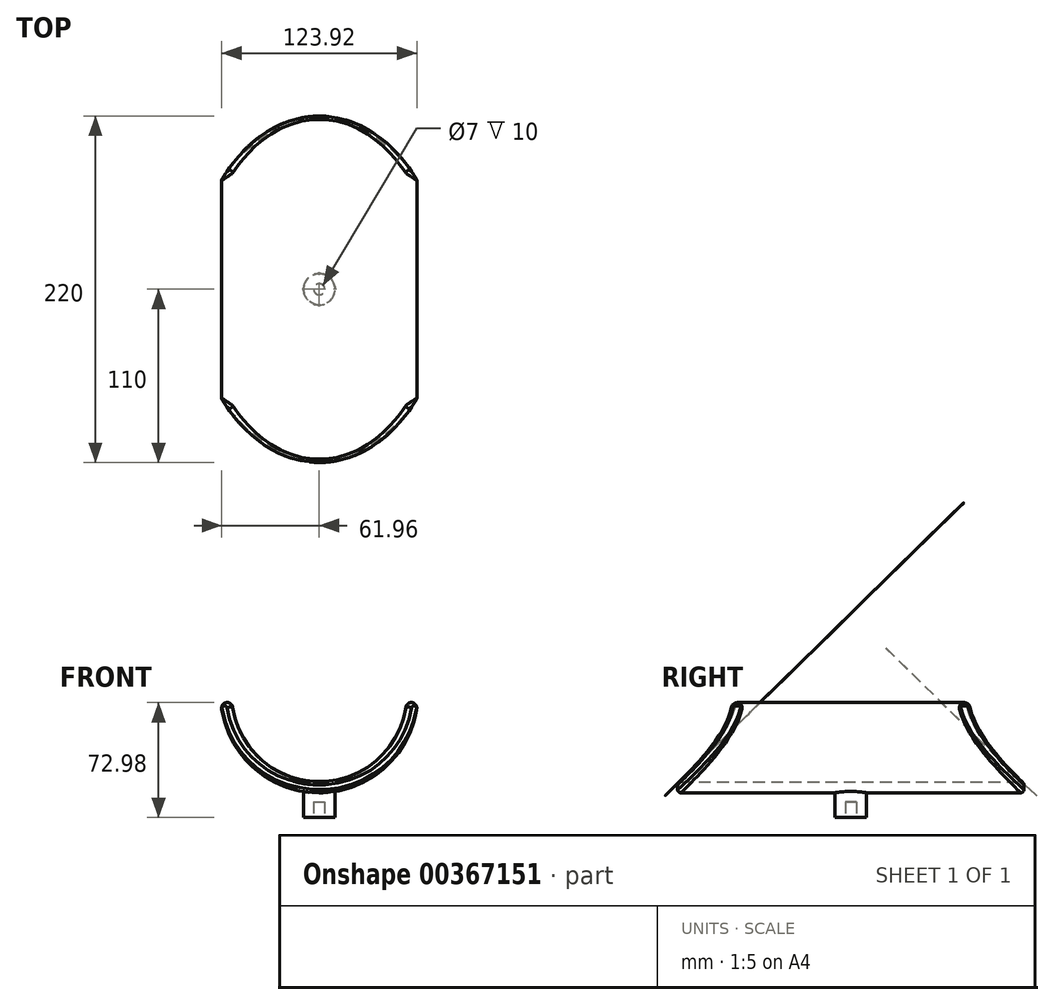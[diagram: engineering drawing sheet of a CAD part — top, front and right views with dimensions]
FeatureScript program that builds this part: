
annotation { "Feature Type Name" : "Feature", "Feature Type Description" : "" }
export const myFeature = defineFeature(function(context is Context, id is Id, definition is map)
    precondition{}
    {
        {
            var Q0;
            Q0=qCreatedBy(makeId("Top.planeOp"),FACE);
            var sketch = newSketch(context, id + "F0", { "sketchPlane" : qUnion([Q0])});
            skEllipse(sketch, "E0", {"center": v(0, 0) * mm, "majorRadius": 110 * mm, "minorRadius": 80 * mm, "majorAxis": v(0, 1)});
            skLineSegment(sketch, "E1", {"start": v(0, 0) * mm, "end": v(0, 110) * mm, "construction": true});
            skLineSegment(sketch, "E2", {"start": v(0, 0) * mm, "end": v(80, 0) * mm, "construction": true});
            skSolve(sketch);
        }
        {
            var Q0;
            Q0 = qSketchRegion(id + "F0", true);
            extrude(context, id + "F1", {"entities" : qUnion([Q0]), "endBound" : BoundingType.SYMMETRIC, "depth" : 150 * mm});
        }
        {
            var Q0;
            Q0=qCreatedBy(makeId("Front.planeOp"),FACE);
            var sketch = newSketch(context, id + "F2", { "sketchPlane" : qUnion([Q0])});
            skLineSegment(sketch, "E3", {"start": v(-80, -75) * mm, "end": v(-80, 75) * mm});
            skLineSegment(sketch, "E4", {"start": v(80, 75) * mm, "end": v(80, -75) * mm});
            skLineSegment(sketch, "E5", {"start": v(-55, 0) * mm, "end": v(55, 0) * mm, "construction": true});
            skArc(sketch, "E6", {"start": v(-55, 0) * mm, "mid": v(0, -47.31) * mm, "end": v(55, 0) * mm});
            skArc(sketch, "E7.0", {"start": v(-61.92, -1.05) * mm, "mid": v(0, -54.31) * mm, "end": v(61.92, -1.05) * mm});
            skArc(sketch, "E8", {"start": v(-61.92, -1.05) * mm, "mid": v(-58.98, 2.94) * mm, "end": v(-55, 0) * mm});
            skArc(sketch, "E9", {"start": v(61.92, -1.05) * mm, "mid": v(58.98, 2.94) * mm, "end": v(55, 0) * mm});
            skSolve(sketch);
        }
        {
            var Q0;
            Q0 = qSketchRegion(id + "F2", true);
            extrude(context, id + "F3", {"entities" : qUnion([Q0]), "operationType" : NewBodyOperationType.INTERSECT, "endBound" : BoundingType.SYMMETRIC, "depth" : 400 * mm});
        }
        {
            var Q0;
            Q0=qCreatedBy(makeId("Top.planeOp"),FACE);
            cPlane(context, id + "F4", {"entities" : qUnion([Q0]), "cplaneType" : CPlaneType.OFFSET, "offset" : 70 * mm, "oppositeDirection" : true, "width" : 150 * mm, "height" : 150 * mm});
        }
        {
            var Q0;
            Q0=qCreatedBy(id+"F4.planeOp",FACE);
            var sketch = newSketch(context, id + "F5", { "sketchPlane" : qUnion([Q0])});
            skCircle(sketch, "E10", {"center": v(0, 0) * mm, "radius": 10 * mm});
            skSolve(sketch);
        }
        {
            var Q0;
            Q0 = qSketchRegion(id + "F5", true);
            var Q1;
            Q1=makeQuery(id+"F1.opExtrude","SWEPT_BODY",BODY,{"disambiguationData":[OSD([sQuery(id+"F0.wireOp",EDGE,"E0")])]});
            extrude(context, id + "F6", {"entities" : qUnion([Q0]), "operationType" : NewBodyOperationType.ADD, "endBound" : BoundingType.UP_TO_BODY, "endBoundEntityBody" : qUnion([Q1]), "depth" : 25 * mm});
        }
        {
            var Q0;
            Q0=makeQuery(id+"F6.opExtrude","CAP_FACE",FACE,{"disambiguationData":[OSD([sQuery(id+"F5.wireOp",EDGE,"E10")])],"isStart":true});
            var sketch = newSketch(context, id + "F7", { "sketchPlane" : qUnion([Q0])});
            skCircle(sketch, "E11", {"center": v(0, 0) * mm, "radius": 3.5 * mm});
            skSolve(sketch);
        }
        {
            var Q0;
            Q0 = qSketchRegion(id + "F7", true);
            extrude(context, id + "F8", {"entities" : qUnion([Q0]), "operationType" : NewBodyOperationType.REMOVE, "oppositeDirection" : true, "depth" : 10 * mm});
        }
        {
            var Q0;
            Q0=makeQuery(id+"F3.boolean.opBoolean","SPLIT",FACE,{"disambiguationData":[OD(0.0)],"derivedFrom":makeQuery(id+"F1.opExtrude","SWEPT_FACE",FACE,{"disambiguationData":[OSD([sQuery(id+"F0.wireOp",EDGE,"E0")])]})});
            var Q1;
            Q1=makeQuery(id+"F3.boolean.opBoolean","SPLIT",FACE,{"disambiguationData":[OD(1.0)],"derivedFrom":makeQuery(id+"F1.opExtrude","SWEPT_FACE",FACE,{"disambiguationData":[OSD([sQuery(id+"F0.wireOp",EDGE,"E0")])]})});
            fillet(context, id + "F9", {"entities" : qUnion([Q0, Q1]), "radius" : 2 * mm, "tangentPropagation" : true, "allowEdgeOverflow" : false});
        }
    });
